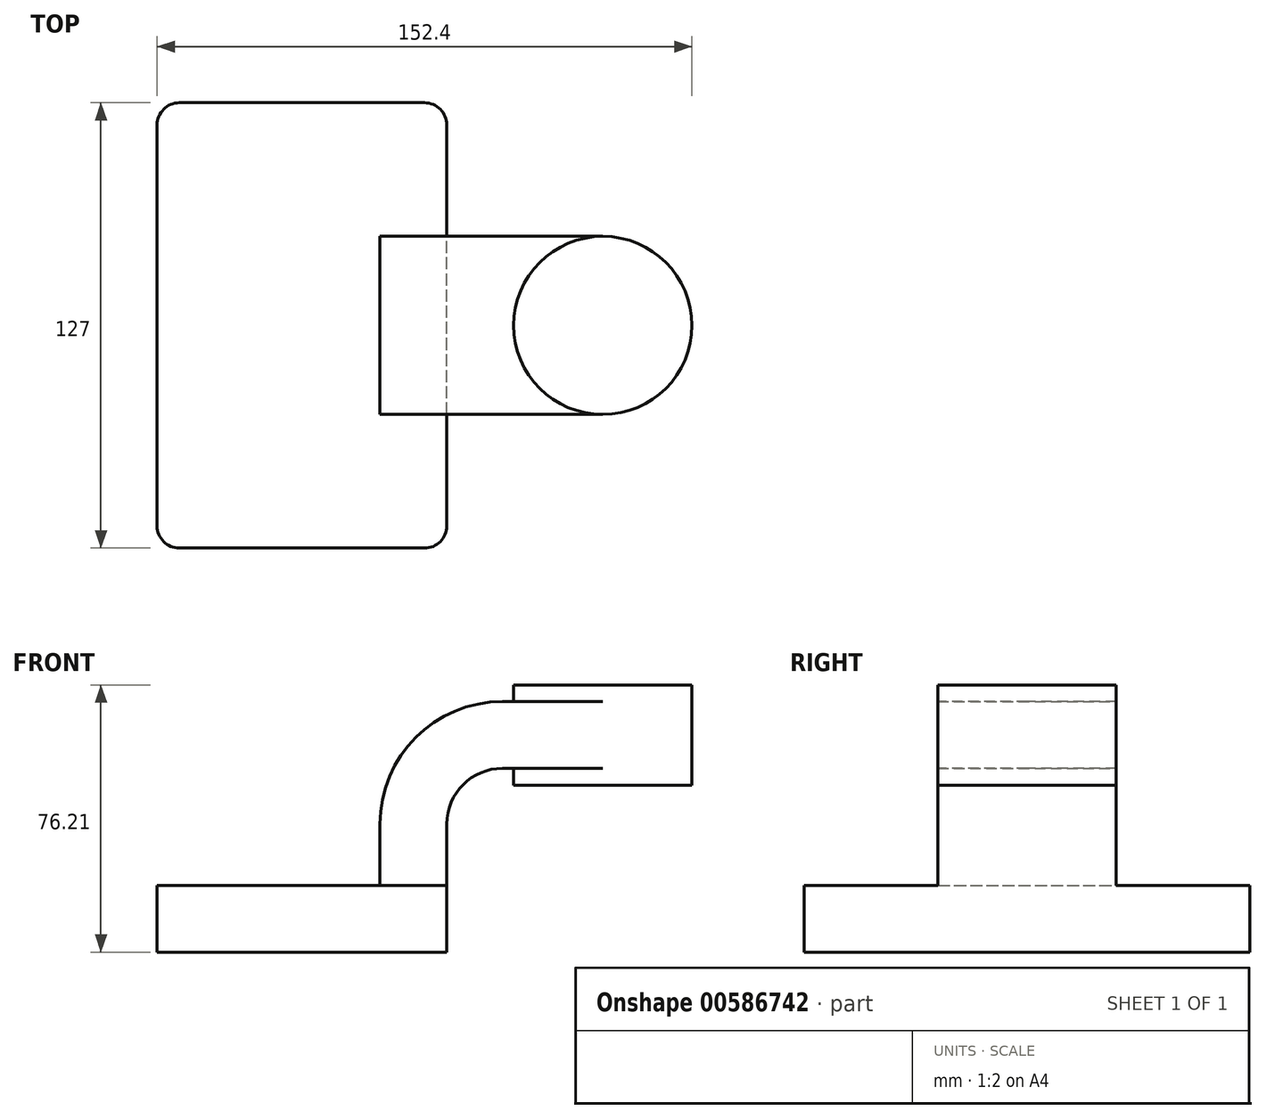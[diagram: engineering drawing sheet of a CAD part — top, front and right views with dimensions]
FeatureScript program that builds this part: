
annotation { "Feature Type Name" : "Feature", "Feature Type Description" : "" }
export const myFeature = defineFeature(function(context is Context, id is Id, definition is map)
    precondition{}
    {
        {
            var Q0;
            Q0=qCreatedBy(makeId("Front.planeOp"),FACE);
            var sketch = newSketch(context, id + "F0", { "sketchPlane" : qUnion([Q0])});
            skLineSegment(sketch, "E0.bottom", {"start": v(-41.28, -9.52) * mm, "end": v(41.28, -9.52) * mm});
            skLineSegment(sketch, "E0.top", {"start": v(-41.28, 9.53) * mm, "end": v(41.28, 9.53) * mm});
            skLineSegment(sketch, "E0.left", {"start": v(-41.28, -9.52) * mm, "end": v(-41.28, 9.53) * mm});
            skLineSegment(sketch, "E0.right", {"start": v(41.28, -9.52) * mm, "end": v(41.28, 9.53) * mm});
            skPoint(sketch, "E0.middle", {"position": v(0, 0) * mm});
            skLineSegment(sketch, "E1.bottom", {"start": v(111.13, 38.1) * mm, "end": v(60.32, 38.1) * mm});
            skLineSegment(sketch, "E1.top", {"start": v(111.13, 66.68) * mm, "end": v(60.33, 66.68) * mm});
            skLineSegment(sketch, "E1.left", {"start": v(111.13, 38.1) * mm, "end": v(111.13, 66.68) * mm});
            skLineSegment(sketch, "E1.right", {"start": v(60.33, 38.1) * mm, "end": v(60.33, 66.68) * mm});
            skPoint(sketch, "E1.middle", {"position": v(85.73, 52.39) * mm});
            skLineSegment(sketch, "E2", {"start": v(41.27, 9.53) * mm, "end": v(41.27, 27) * mm});
            skArc(sketch, "E3", {"start": v(41.27, 27) * mm, "mid": v(45.92, 38.23) * mm, "end": v(57.15, 42.88) * mm});
            skLineSegment(sketch, "E4", {"start": v(57.15, 42.88) * mm, "end": v(85.73, 42.88) * mm});
            skLineSegment(sketch, "E5.0", {"start": v(57.15, 61.93) * mm, "end": v(85.73, 61.93) * mm});
            skArc(sketch, "E5.1", {"start": v(22.22, 27) * mm, "mid": v(32.45, 51.7) * mm, "end": v(57.15, 61.93) * mm});
            skLineSegment(sketch, "E5.2", {"start": v(22.22, 9.53) * mm, "end": v(22.22, 27) * mm});
            skPoint(sketch, "E6", {"position": v(85.73, 38.1) * mm});
            skLineSegment(sketch, "E7", {"start": v(85.73, 38.1) * mm, "end": v(85.73, 66.68) * mm});
            skFitSpline(sketch, "E8", {"points": [v(-41.28, 9.53) * mm, v(57.15, 61.93) * mm], "startDerivative": vector(0.83, 69.24) * mm, "endDerivative": vector(136.33, -0.29) * mm});
            skSolve(sketch);
        }
        {
            var Q0;
            Q0=makeQuery(id+"F0.imprint","IMPRINT",FACE,{"disambiguationData":[TD([[makeQuery(id+"F0.imprint","IMPRINT",EDGE,{"derivedFrom":sQuery(id+"F0.wireOp",EDGE,"E0.bottom")}),1.0]])]});
            extrude(context, id + "F1", {"entities" : qUnion([Q0]), "endBound" : BoundingType.SYMMETRIC, "depth" : 127 * mm, "offsetDistance" : 25.4 * mm});
        }
        {
            var Q0;
            {var subQ1=sQuery(id+"F0.wireOp",EDGE,"E2");Q0=makeQuery(id+"F0.imprint","IMPRINT",FACE,{"disambiguationData":[TD([[makeQuery(id+"F0.imprint","IMPRINT",EDGE,{"derivedFrom":subQ1}),1.0]])]});}
            var Q1;
            {var subQ0=sQuery(id+"F0.wireOp",EDGE,"E4");var subQ1=sQuery(id+"F0.wireOp",EDGE,"E1.right");var subQ2=makeQuery(id+"F0.imprint","INTERSECT",VERTEX,{"derivedFrom":[subQ1,subQ0]});Q1=makeQuery(id+"F0.imprint","IMPRINT",FACE,{"disambiguationData":[TD([[makeQuery(id+"F0.imprint","IMPRINT",EDGE,{"disambiguationData":[TD([[subQ2,-1.0]])],"derivedFrom":subQ1}),-1.0]])]});}
            extrude(context, id + "F2", {"entities" : qUnion([Q0, Q1]), "operationType" : NewBodyOperationType.ADD, "endBound" : BoundingType.SYMMETRIC, "depth" : 50.8 * mm, "offsetDistance" : 25.4 * mm});
        }
        {
            var Q0;
            Q0=makeQuery(id+"F0.imprint","IMPRINT",FACE,{"disambiguationData":[TD([[makeQuery(id+"F0.imprint","IMPRINT",EDGE,{"derivedFrom":sQuery(id+"F0.wireOp",EDGE,"E5.1")}),1.0]])]});
            extrude(context, id + "F3", {"entities" : qUnion([Q0]), "operationType" : NewBodyOperationType.ADD, "endBound" : BoundingType.SYMMETRIC, "depth" : 15.88 * mm, "offsetDistance" : 25.4 * mm});
        }
        {
            var Q0;
            {var subQ4=sQuery(id+"F0.wireOp",EDGE,"E1.left");Q0=makeQuery(id+"F0.imprint","IMPRINT",FACE,{"disambiguationData":[TD([[makeQuery(id+"F0.imprint","IMPRINT",EDGE,{"derivedFrom":subQ4}),1.0]])]});}
            var Q1;
            Q1=sQuery(id+"F0.wireOp",EDGE,"E7");
            revolve(context, id + "F4", {"operationType" : NewBodyOperationType.ADD, "entities" : qUnion([Q0]), "axis" : qUnion([Q1]), "revolveType" : RevolveType.FULL});
        }
        {
            var Q0;
            Q0=makeQuery(id+"F1.opExtrude","CAP_EDGE",EDGE,{"disambiguationData":[OSD([sQuery(id+"F0.wireOp",EDGE,"E0.right")])],"isStart":false});
            var Q1;
            Q1=makeQuery(id+"F1.opExtrude","CAP_EDGE",EDGE,{"disambiguationData":[OSD([sQuery(id+"F0.wireOp",EDGE,"E0.left")])],"isStart":false});
            var Q2;
            Q2=makeQuery(id+"F1.opExtrude","CAP_EDGE",EDGE,{"disambiguationData":[OSD([sQuery(id+"F0.wireOp",EDGE,"E0.right")])],"isStart":true});
            var Q3;
            Q3=makeQuery(id+"F1.opExtrude","CAP_EDGE",EDGE,{"disambiguationData":[OSD([sQuery(id+"F0.wireOp",EDGE,"E0.left")])],"isStart":true});
            fillet(context, id + "F5", {"entities" : qUnion([Q0, Q1, Q2, Q3]), "radius" : 6.35 * mm, "tangentPropagation" : true, "allowEdgeOverflow" : false});
        }
    });
